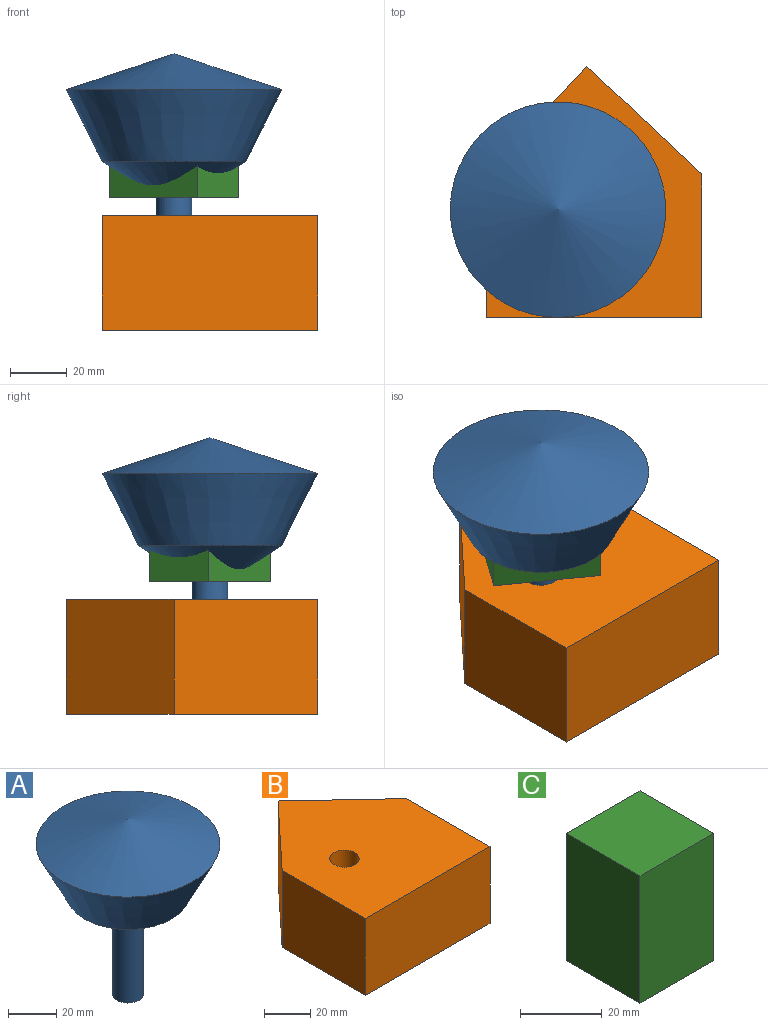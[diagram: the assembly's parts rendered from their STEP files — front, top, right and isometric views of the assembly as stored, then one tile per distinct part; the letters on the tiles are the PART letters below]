
ASSEMBLY  parts=3 mates=2
PART A: 5 faces, bbox 76.2x76.2x88.9 mm
  f0: plane 12.7x12.7mm, normal (0,0,-1), area 126.7mm2, adj f1
  f1: cylinder r=6.35mm len=38.1mm, axis (0,0,-1), area 1520.1mm2, adj f0,f2
  f2: cone r=25.4mm half-angle=56.3deg, axis (0,0,1), area 2283.7mm2, adj f1,f3
  f3: cone r=38.1mm half-angle=26.6deg, axis (0,0,1), area 5665.2mm2, adj f2,f4
  f4: cone r=0mm half-angle=71.6deg, axis (0,0,-1), area 4807mm2, adj f3
PART B: 8 faces, bbox 76.2x88.9x40.6 mm
  f0: plane 50.8x40.64mm, normal (1,0,0), area 2064.5mm2, adj f1,f4,f5,f6
  f1: plane 40.64x40.64mm, normal (0.68,0.73,0), area 2263.9mm2, adj f0,f2,f5,f6
  f2: plane 40.64x38.1mm, normal (-0.73,0.68,0), area 2118mm2, adj f1,f3,f5,f6
  f3: plane 50.8x40.64mm, normal (-1,0,0), area 2064.5mm2, adj f2,f4,f5,f6
  f4: plane 76.2x40.64mm, normal (0,-1,0), area 3096.8mm2, adj f0,f3,f5,f6
  f5: plane 88.9x76.2mm, normal (0,0,1), area 5195.9mm2, adj f0,f1,f2,f3,f4,f7
  f6: plane 88.9x76.2mm, normal (0,0,-1), area 5195.9mm2, adj f0,f1,f2,f3,f4,f7
  f7: cylinder r=6.35mm len=40.64mm, axis (0,0,1), area 1621.5mm2, adj f5,f6
PART C: 6 faces, bbox 25.4x25.4x38.1 mm
  f0: plane 25.4x25.4mm, normal (0,0,1), area 645.2mm2, adj f1,f3,f4,f5
  f1: plane 38.1x25.4mm, normal (-1,0,0), area 967.7mm2, adj f0,f2,f4,f5
  f2: plane 25.4x25.4mm, normal (0,0,-1), area 645.2mm2, adj f1,f3,f4,f5
  f3: plane 38.1x25.4mm, normal (1,0,0), area 967.7mm2, adj f0,f2,f4,f5
  f4: plane 38.1x25.4mm, normal (0,-1,0), area 967.7mm2, adj f0,f1,f2,f3
  f5: plane 38.1x25.4mm, normal (0,1,0), area 967.7mm2, adj f0,f1,f2,f3
PLACE A rot(axis=(0,0,1),54.6deg) t=(28.38,33.43,12.66)mm
PLACE B t=(2.98,-4.67,3.77)mm fixed
PLACE C rot(axis=(-0.34,0.66,-0.66),142.2deg) t=(49.66,96.22,50.76)mm
MATE fastened C.f4 <-> A.f1  axis (0,0,1) through (28.38,33.43,76.16)mm
MATE revolute A.f1 <-> B.f7  axis (0,0,-1) through (28.38,33.43,31.71)mm
